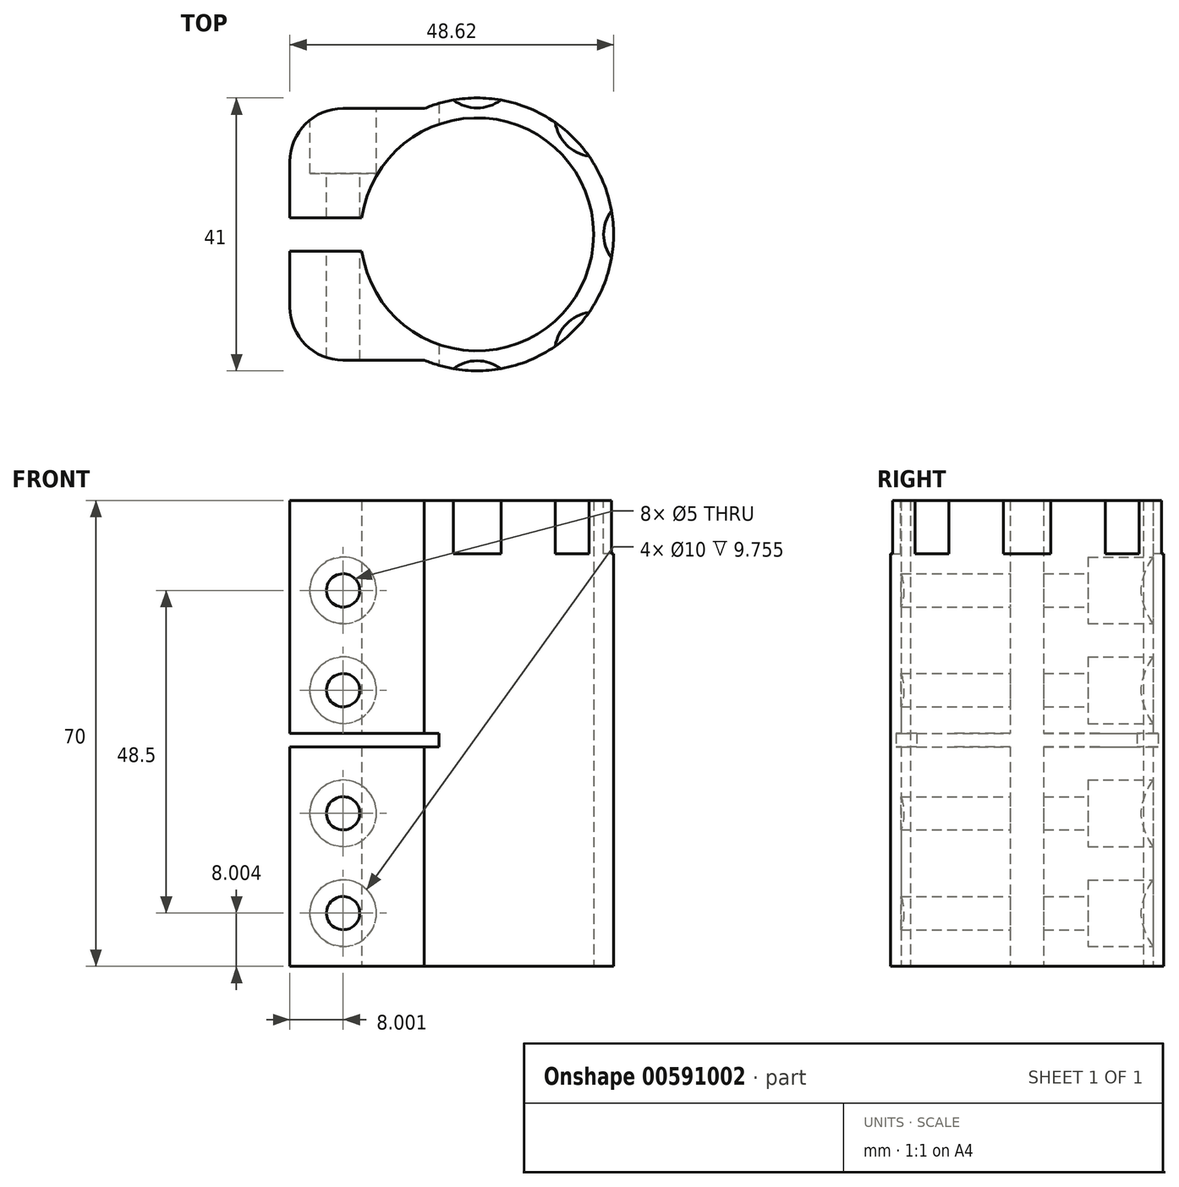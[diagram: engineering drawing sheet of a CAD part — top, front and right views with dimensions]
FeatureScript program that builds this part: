
annotation { "Feature Type Name" : "Feature", "Feature Type Description" : "" }
export const myFeature = defineFeature(function(context is Context, id is Id, definition is map)
    precondition{}
    {
        {
            var Q0;
            Q0=qCreatedBy(makeId("Top.planeOp"),FACE);
            var sketch = newSketch(context, id + "F0", { "sketchPlane" : qUnion([Q0])});
            skArc(sketch, "E0", {"start": v(-17.32, -2.5) * mm, "mid": v(17.5, 0) * mm, "end": v(-17.32, 2.5) * mm});
            skLineSegment(sketch, "E1", {"start": v(-7.92, 18.9) * mm, "end": v(-20.12, 18.9) * mm});
            skLineSegment(sketch, "E2", {"start": v(-28.12, 10.9) * mm, "end": v(-28.12, 2.5) * mm});
            skLineSegment(sketch, "E3", {"start": v(-28.12, 2.5) * mm, "end": v(-17.32, 2.5) * mm});
            skPoint(sketch, "E4.visualSharp", {"position": v(-28.12, 18.9) * mm});
            skArc(sketch, "E4.filletArc", {"start": v(-20.12, 18.9) * mm, "mid": v(-25.78, 16.57) * mm, "end": v(-28.12, 10.9) * mm});
            skLineSegment(sketch, "E5", {"start": v(0, 0) * mm, "end": v(57.83, 0) * mm, "construction": true});
            skLineSegment(sketch, "E6.MirrorCS", {"start": v(-28.12, -2.5) * mm, "end": v(-17.32, -2.5) * mm});
            skLineSegment(sketch, "E7.MirrorCS", {"start": v(-7.92, -18.9) * mm, "end": v(-20.12, -18.9) * mm});
            skLineSegment(sketch, "E8.MirrorCS", {"start": v(-28.12, -10.9) * mm, "end": v(-28.12, -2.5) * mm});
            skArc(sketch, "E9.MirrorCS", {"start": v(-20.12, -18.9) * mm, "mid": v(-25.78, -16.57) * mm, "end": v(-28.12, -10.9) * mm});
            skArc(sketch, "E10.trimOffspring", {"start": v(-7.92, -18.9) * mm, "mid": v(20.5, 0) * mm, "end": v(-7.92, 18.9) * mm});
            skSolve(sketch);
        }
        {
            var Q0;
            Q0 = qSketchRegion(id + "F0", true);
            extrude(context, id + "F1", {"entities" : qUnion([Q0]), "endBound" : BoundingType.SYMMETRIC, "depth" : 70 * mm, "offsetDistance" : 25 * mm});
        }
        {
            var Q0;
            Q0=makeQuery(id+"F1.opExtrude","SWEPT_FACE",FACE,{"disambiguationData":[OSD([sQuery(id+"F0.wireOp",EDGE,"E1")])]});
            var sketch = newSketch(context, id + "F2", { "sketchPlane" : qUnion([Q0])});
            skPoint(sketch, "E11", {"position": v(20.12, -27) * mm});
            skPoint(sketch, "E12", {"position": v(20.12, -12) * mm});
            skPoint(sketch, "E13", {"position": v(20.12, 6.5) * mm});
            skPoint(sketch, "E14", {"position": v(20.12, 21.5) * mm});
            skSolve(sketch);
        }
        {
            var Q0;
            Q0=sQuery(id+"F2.wireOp",VERTEX,"E14");
            var Q1;
            Q1=sQuery(id+"F2.wireOp",VERTEX,"E13");
            var Q2;
            Q2=sQuery(id+"F2.wireOp",VERTEX,"E11");
            var Q3;
            Q3=sQuery(id+"F2.wireOp",VERTEX,"E12");
            var Q4;
            Q4=makeQuery(id+"F1.opExtrude","SWEPT_BODY",BODY,{"disambiguationData":[OSD([sQuery(id+"F0.wireOp",EDGE,"E0"),sQuery(id+"F0.wireOp",EDGE,"E1"),sQuery(id+"F0.wireOp",EDGE,"E2"),sQuery(id+"F0.wireOp",EDGE,"E3"),sQuery(id+"F0.wireOp",EDGE,"E4.filletArc"),sQuery(id+"F0.wireOp",EDGE,"E6.MirrorCS"),sQuery(id+"F0.wireOp",EDGE,"E7.MirrorCS"),sQuery(id+"F0.wireOp",EDGE,"E8.MirrorCS"),sQuery(id+"F0.wireOp",EDGE,"E9.MirrorCS"),sQuery(id+"F0.wireOp",EDGE,"E10.trimOffspring")])]});
            hole(context, id + "F3", {"style" : HoleStyle.C_BORE, "endStyle" : HoleEndStyle.THROUGH, "holeDiameter" : 5 * mm, "cBoreDiameter" : 10 * mm, "cBoreDepth" : 8 * mm, "majorDiameter" : 5 * mm, "isTappedThrough" : true, "tappedDepth" : 12 * mm, "tapClearance" : 3, "locations" : qUnion([Q0, Q1, Q2, Q3]), "scope" : qUnion([Q4])});
        }
        {
            var Q0;
            Q0=qCreatedBy(makeId("Front.planeOp"),FACE);
            var sketch = newSketch(context, id + "F4", { "sketchPlane" : qUnion([Q0])});
            skSolve(sketch);
        }
        {
            var Q0;
            Q0=qCreatedBy(makeId("Front.planeOp"),FACE);
            var sketch = newSketch(context, id + "F5", { "sketchPlane" : qUnion([Q0])});
            skLineSegment(sketch, "E15.bottom", {"start": v(-28.12, -2) * mm, "end": v(-5.72, -2) * mm});
            skLineSegment(sketch, "E15.top", {"start": v(-28.12, 0) * mm, "end": v(-5.72, 0) * mm});
            skLineSegment(sketch, "E15.left", {"start": v(-28.12, -2) * mm, "end": v(-28.12, 0) * mm});
            skLineSegment(sketch, "E15.right", {"start": v(-5.72, -2) * mm, "end": v(-5.72, 0) * mm});
            skSolve(sketch);
        }
        {
            var Q0;
            Q0 = qSketchRegion(id + "F4", true);
            var Q1;
            Q1=makeQuery(id+"F5.imprint","IMPRINT",FACE,{"disambiguationData":[TD([[makeQuery(id+"F5.imprint","IMPRINT",EDGE,{"derivedFrom":sQuery(id+"F5.wireOp",EDGE,"E15.bottom")}),1.0]])]});
            extrude(context, id + "F6", {"entities" : qUnion([Q0, Q1]), "operationType" : NewBodyOperationType.REMOVE, "endBound" : BoundingType.SYMMETRIC, "oppositeDirection" : true, "depth" : 50 * mm, "offsetDistance" : 25 * mm});
        }
        {
            var Q0;
            Q0=makeQuery(id+"F1.opExtrude","CAP_FACE",FACE,{"disambiguationData":[OSD([sQuery(id+"F0.wireOp",EDGE,"E0"),sQuery(id+"F0.wireOp",EDGE,"E1"),sQuery(id+"F0.wireOp",EDGE,"E2"),sQuery(id+"F0.wireOp",EDGE,"E3"),sQuery(id+"F0.wireOp",EDGE,"E4.filletArc"),sQuery(id+"F0.wireOp",EDGE,"E6.MirrorCS"),sQuery(id+"F0.wireOp",EDGE,"E7.MirrorCS"),sQuery(id+"F0.wireOp",EDGE,"E8.MirrorCS"),sQuery(id+"F0.wireOp",EDGE,"E9.MirrorCS"),sQuery(id+"F0.wireOp",EDGE,"E10.trimOffspring")])],"isStart":false});
            var sketch = newSketch(context, id + "F7", { "sketchPlane" : qUnion([Q0])});
            skCircle(sketch, "E16", {"center": v(0, -25) * mm, "radius": 6 * mm});
            skCircle(sketch, "E17.1.0", {"center": v(17.68, -17.68) * mm, "radius": 6 * mm});
            skCircle(sketch, "E17.2.0", {"center": v(25, 0) * mm, "radius": 6 * mm});
            skCircle(sketch, "E17.3.0", {"center": v(17.68, 17.68) * mm, "radius": 6 * mm});
            skCircle(sketch, "E17.4.0", {"center": v(0, 25) * mm, "radius": 6 * mm});
            skPoint(sketch, "E17.center", {"position": v(0, 0) * mm});
            skLineSegment(sketch, "E17.anchor1", {"start": v(0, 0) * mm, "end": v(0, -25) * mm, "construction": true});
            skLineSegment(sketch, "E17.anchor2", {"start": v(0, 0) * mm, "end": v(0, 25) * mm, "construction": true});
            skSolve(sketch);
        }
        {
            var Q0;
            Q0 = qSketchRegion(id + "F7", true);
            extrude(context, id + "F8", {"entities" : qUnion([Q0]), "operationType" : NewBodyOperationType.REMOVE, "oppositeDirection" : true, "depth" : 8 * mm, "offsetDistance" : 25 * mm});
        }
    });
